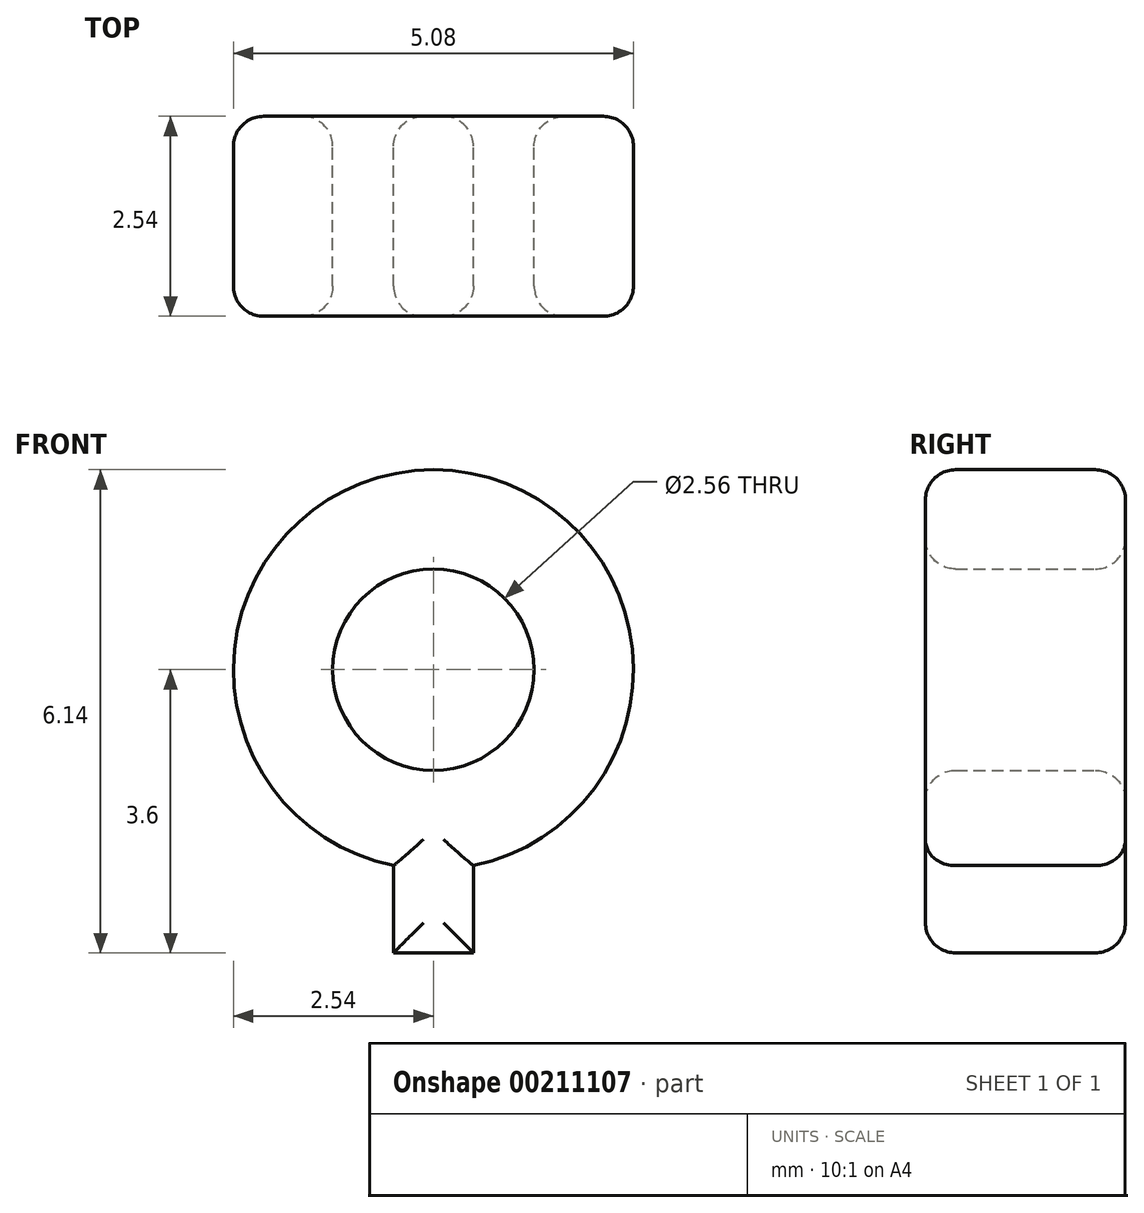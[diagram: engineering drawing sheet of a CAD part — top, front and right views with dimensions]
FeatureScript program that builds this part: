
annotation { "Feature Type Name" : "Feature", "Feature Type Description" : "" }
export const myFeature = defineFeature(function(context is Context, id is Id, definition is map)
    precondition{}
    {
        {
            var Q0;
            Q0=qCreatedBy(makeId("Front.planeOp"),FACE);
            var sketch = newSketch(context, id + "F0", { "sketchPlane" : qUnion([Q0])});
            skArc(sketch, "E0", {"start": v(0.5, -2.49) * mm, "mid": v(0, 2.54) * mm, "end": v(-0.5, -2.49) * mm});
            skCircle(sketch, "E1", {"center": v(0, 0) * mm, "radius": 1.28 * mm});
            skLineSegment(sketch, "E2.0", {"start": v(-0.5, -2.49) * mm, "end": v(-0.5, -3.6) * mm});
            skLineSegment(sketch, "E3.0", {"start": v(0.5, -2.49) * mm, "end": v(0.5, -3.6) * mm});
            skLineSegment(sketch, "E4", {"start": v(-0.5, -3.6) * mm, "end": v(0.5, -3.6) * mm});
            skPoint(sketch, "E5.start.orphan", {"position": v(0, -1.28) * mm});
            skSolve(sketch);
        }
        {
            var Q0;
            Q0=makeQuery(id+"F0.imprint","IMPRINT",FACE,{"disambiguationData":[TD([[makeQuery(id+"F0.imprint","IMPRINT",EDGE,{"derivedFrom":sQuery(id+"F0.wireOp",EDGE,"E0")}),1.0]])]});
            extrude(context, id + "F1", {"entities" : qUnion([Q0]), "depth" : 2.54 * mm});
        }
        {
            var Q0;
            Q0=makeQuery(id+"F1.opExtrude","CAP_FACE",FACE,{"disambiguationData":[OSD([sQuery(id+"F0.wireOp",EDGE,"E0"),sQuery(id+"F0.wireOp",EDGE,"E1"),sQuery(id+"F0.wireOp",EDGE,"E2.0"),sQuery(id+"F0.wireOp",EDGE,"E3.0"),sQuery(id+"F0.wireOp",EDGE,"E4")])],"isStart":false});
            var Q1;
            Q1=makeQuery(id+"F1.opExtrude","CAP_FACE",FACE,{"disambiguationData":[OSD([sQuery(id+"F0.wireOp",EDGE,"E0"),sQuery(id+"F0.wireOp",EDGE,"E1"),sQuery(id+"F0.wireOp",EDGE,"E2.0"),sQuery(id+"F0.wireOp",EDGE,"E3.0"),sQuery(id+"F0.wireOp",EDGE,"E4")])],"isStart":true});
            fillet(context, id + "F2", {"entities" : qUnion([Q0, Q1]), "radius" : 0.38 * mm, "tangentPropagation" : true, "allowEdgeOverflow" : false});
        }
    });
